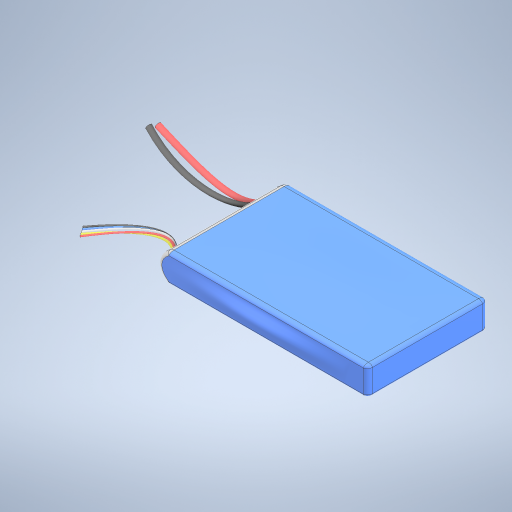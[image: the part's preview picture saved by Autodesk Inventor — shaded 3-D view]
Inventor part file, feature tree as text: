
AUTODESK INVENTOR PART (.ipt)
format: ipt  version: 2024.3 (Build 283343000, 343)  size: 638,976 bytes
history: native  units: in
note: dims shown in document units (in); Inventor stores cm internally (conversion verified against a paired STEP export)
features: other x3, direct_edit x1, sweep x1
ambient origin geometry x8: Origin, YZ Plane, XZ Plane, XY Plane, X Axis, Y Axis, Z Axis, Center Point
bodies: Solid1 (feature_tree)
feature tree (5):
  other  "Plane1"
  other  "Plane2"
  direct_edit  "Direct Edit1"
  sweep  "Sweep7"
  other  "Scale1"
